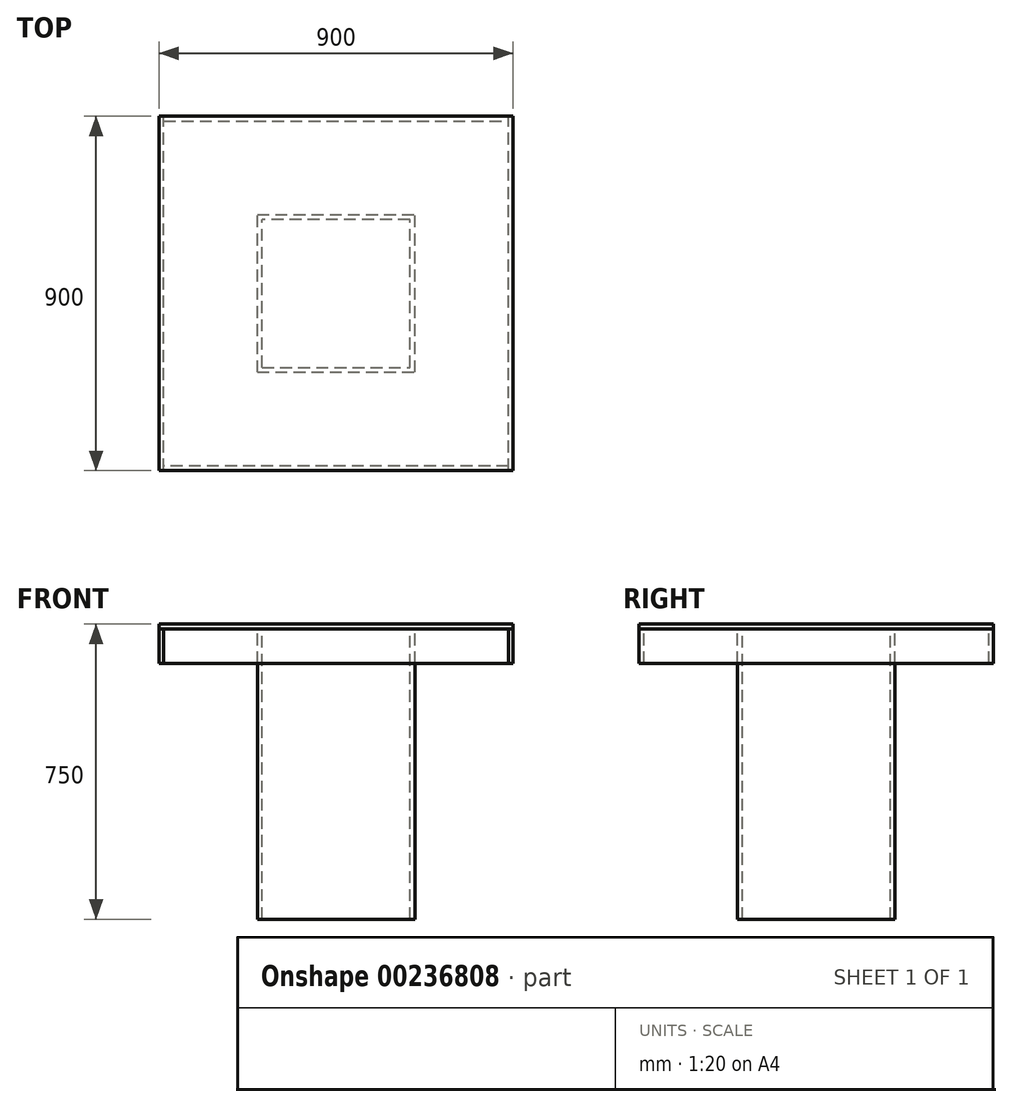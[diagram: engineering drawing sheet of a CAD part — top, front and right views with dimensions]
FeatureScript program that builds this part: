
annotation { "Feature Type Name" : "Feature", "Feature Type Description" : "" }
export const myFeature = defineFeature(function(context is Context, id is Id, definition is map)
    precondition{}
    {
        {
            var Q0;
            Q0=qCreatedBy(makeId("Top.planeOp"),FACE);
            var sketch = newSketch(context, id + "F0", { "sketchPlane" : qUnion([Q0])});
            skLineSegment(sketch, "E0.bottom", {"start": v(-450, -450) * mm, "end": v(450, -450) * mm});
            skLineSegment(sketch, "E0.top", {"start": v(-450, 450) * mm, "end": v(450, 450) * mm});
            skLineSegment(sketch, "E0.left", {"start": v(-450, -450) * mm, "end": v(-450, 450) * mm});
            skLineSegment(sketch, "E0.right", {"start": v(450, -450) * mm, "end": v(450, 450) * mm});
            skPoint(sketch, "E0.middle", {"position": v(0, 0) * mm});
            skSolve(sketch);
        }
        {
            var Q0;
            Q0 = qSketchRegion(id + "F0", true);
            extrude(context, id + "F1", {"entities" : qUnion([Q0]), "depth" : 12 * mm});
        }
        {
            var Q0;
            Q0=makeQuery(id+"F1.opExtrude","CAP_FACE",FACE,{"disambiguationData":[OSD([sQuery(id+"F0.wireOp",EDGE,"E0.bottom"),sQuery(id+"F0.wireOp",EDGE,"E0.top"),sQuery(id+"F0.wireOp",EDGE,"E0.left"),sQuery(id+"F0.wireOp",EDGE,"E0.right")])],"isStart":true});
            var sketch = newSketch(context, id + "F2", { "sketchPlane" : qUnion([Q0])});
            skLineSegment(sketch, "E1.bottom", {"start": v(-450, 450) * mm, "end": v(-438, 450) * mm});
            skLineSegment(sketch, "E1.top", {"start": v(-450, -450) * mm, "end": v(-438, -450) * mm});
            skLineSegment(sketch, "E1.left", {"start": v(-450, 450) * mm, "end": v(-450, -450) * mm});
            skLineSegment(sketch, "E1.right", {"start": v(-438, 450) * mm, "end": v(-438, -450) * mm});
            skLineSegment(sketch, "E2.bottom", {"start": v(450, 450) * mm, "end": v(438, 450) * mm});
            skLineSegment(sketch, "E2.top", {"start": v(450, -450) * mm, "end": v(438, -450) * mm});
            skLineSegment(sketch, "E2.left", {"start": v(450, 450) * mm, "end": v(450, -450) * mm});
            skLineSegment(sketch, "E2.right", {"start": v(438, 450) * mm, "end": v(438, -450) * mm});
            skLineSegment(sketch, "E3.bottom", {"start": v(438, 438) * mm, "end": v(-438, 438) * mm});
            skLineSegment(sketch, "E3.top", {"start": v(438, 450) * mm, "end": v(-438, 450) * mm});
            skLineSegment(sketch, "E3.left", {"start": v(438, 438) * mm, "end": v(438, 450) * mm});
            skLineSegment(sketch, "E3.right", {"start": v(-438, 438) * mm, "end": v(-438, 450) * mm});
            skLineSegment(sketch, "E4.bottom", {"start": v(-438, -438) * mm, "end": v(438, -438) * mm});
            skLineSegment(sketch, "E4.top", {"start": v(-438, -450) * mm, "end": v(438, -450) * mm});
            skLineSegment(sketch, "E4.left", {"start": v(-438, -438) * mm, "end": v(-438, -450) * mm});
            skLineSegment(sketch, "E4.right", {"start": v(438, -438) * mm, "end": v(438, -450) * mm});
            skSolve(sketch);
        }
        {
            var Q0;
            Q0=makeQuery(id+"F2.imprint","IMPRINT",FACE,{"disambiguationData":[TD([[makeQuery(id+"F2.imprint","IMPRINT",EDGE,{"derivedFrom":sQuery(id+"F2.wireOp",EDGE,"E1.bottom")}),-1.0]])]});
            extrude(context, id + "F3", {"entities" : qUnion([Q0]), "depth" : 88 * mm});
        }
        {
            var Q0;
            Q0=makeQuery(id+"F2.imprint","IMPRINT",FACE,{"disambiguationData":[TD([[makeQuery(id+"F2.imprint","IMPRINT",EDGE,{"derivedFrom":sQuery(id+"F2.wireOp",EDGE,"E3.bottom")}),-1.0]])]});
            extrude(context, id + "F4", {"entities" : qUnion([Q0]), "depth" : 88 * mm});
        }
        {
            var Q0;
            Q0=makeQuery(id+"F2.imprint","IMPRINT",FACE,{"disambiguationData":[TD([[makeQuery(id+"F2.imprint","IMPRINT",EDGE,{"derivedFrom":sQuery(id+"F2.wireOp",EDGE,"E2.bottom")}),-1.0]])]});
            extrude(context, id + "F5", {"entities" : qUnion([Q0]), "depth" : 88 * mm});
        }
        {
            var Q0;
            Q0=makeQuery(id+"F2.imprint","IMPRINT",FACE,{"disambiguationData":[TD([[makeQuery(id+"F2.imprint","IMPRINT",EDGE,{"derivedFrom":sQuery(id+"F2.wireOp",EDGE,"E4.bottom")}),-1.0]])]});
            extrude(context, id + "F6", {"entities" : qUnion([Q0]), "depth" : 88 * mm});
        }
        {
            var Q0;
            Q0=makeQuery(id+"F2.imprint","IMPRINT",FACE,{"disambiguationData":[TD([[makeQuery(id+"F2.imprint","IMPRINT",EDGE,{"derivedFrom":sQuery(id+"F2.wireOp",EDGE,"E1.right")}),1.0]])]});
            var sketch = newSketch(context, id + "F7", { "sketchPlane" : qUnion([Q0])});
            skLineSegment(sketch, "E5.bottom", {"start": v(-200, 200) * mm, "end": v(-188, 200) * mm});
            skLineSegment(sketch, "E5.top", {"start": v(-200, -200) * mm, "end": v(-188, -200) * mm});
            skLineSegment(sketch, "E5.left", {"start": v(-200, 200) * mm, "end": v(-200, -200) * mm});
            skLineSegment(sketch, "E5.right", {"start": v(-188, 200) * mm, "end": v(-188, -200) * mm});
            skLineSegment(sketch, "E6.bottom", {"start": v(-188, 200) * mm, "end": v(188, 200) * mm});
            skLineSegment(sketch, "E6.top", {"start": v(-188, 188) * mm, "end": v(188, 188) * mm});
            skLineSegment(sketch, "E6.left", {"start": v(-188, 200) * mm, "end": v(-188, 188) * mm});
            skLineSegment(sketch, "E6.right", {"start": v(188, 200) * mm, "end": v(188, 188) * mm});
            skLineSegment(sketch, "E7.bottom", {"start": v(188, 200) * mm, "end": v(200, 200) * mm});
            skLineSegment(sketch, "E7.top", {"start": v(188, -200) * mm, "end": v(200, -200) * mm});
            skLineSegment(sketch, "E7.left", {"start": v(188, 200) * mm, "end": v(188, -200) * mm});
            skLineSegment(sketch, "E7.right", {"start": v(200, 200) * mm, "end": v(200, -200) * mm});
            skLineSegment(sketch, "E8.bottom", {"start": v(188, -200) * mm, "end": v(-188, -200) * mm});
            skLineSegment(sketch, "E8.top", {"start": v(188, -188) * mm, "end": v(-188, -188) * mm});
            skLineSegment(sketch, "E8.left", {"start": v(188, -200) * mm, "end": v(188, -188) * mm});
            skLineSegment(sketch, "E8.right", {"start": v(-188, -200) * mm, "end": v(-188, -188) * mm});
            skSolve(sketch);
        }
        {
            var Q0;
            Q0 = qSketchRegion(id + "F7", true);
            extrude(context, id + "F8", {"entities" : qUnion([Q0]), "operationType" : NewBodyOperationType.ADD, "depth" : 738 * mm});
        }
    });
